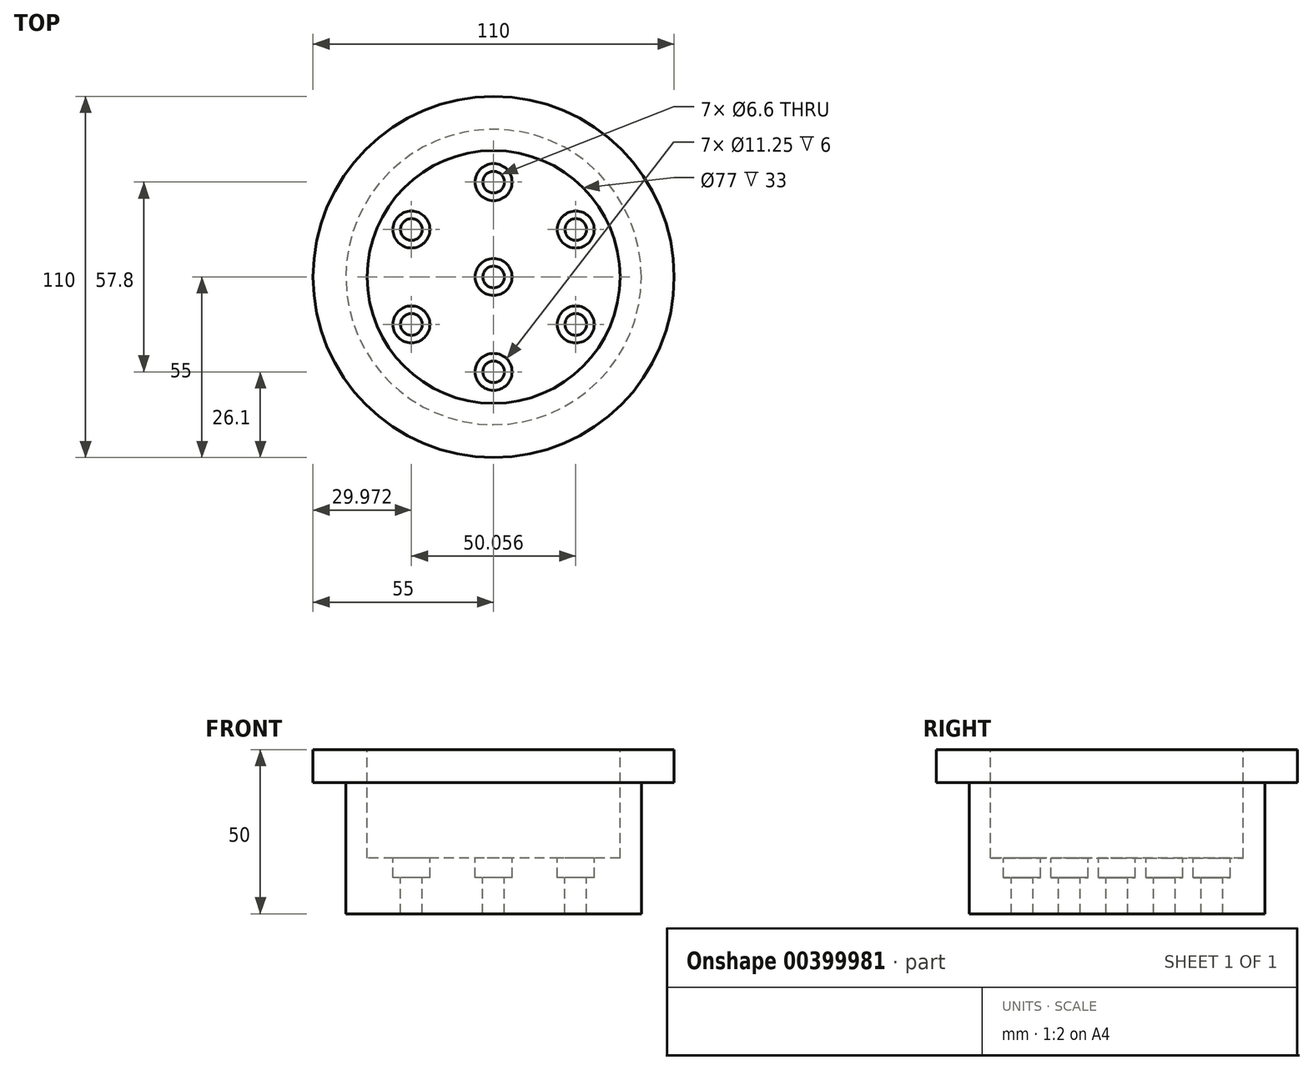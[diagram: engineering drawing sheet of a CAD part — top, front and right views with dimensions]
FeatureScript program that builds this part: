
annotation { "Feature Type Name" : "Feature", "Feature Type Description" : "" }
export const myFeature = defineFeature(function(context is Context, id is Id, definition is map)
    precondition{}
    {
        {
            var Q0;
            Q0=qCreatedBy(makeId("Top.planeOp"),FACE);
            var sketch = newSketch(context, id + "F0", { "sketchPlane" : qUnion([Q0])});
            skCircle(sketch, "E0", {"center": v(0, 0) * mm, "radius": 55 * mm});
            skCircle(sketch, "E1.cCircle", {"center": v(0, 0) * mm, "radius": 25.03 * mm, "construction": true});
            skLineSegment(sketch, "E1.0", {"start": v(25.03, -14.45) * mm, "end": v(0, -28.9) * mm});
            skLineSegment(sketch, "E1.1", {"start": v(0, -28.9) * mm, "end": v(-25.03, -14.45) * mm});
            skLineSegment(sketch, "E1.2", {"start": v(-25.03, -14.45) * mm, "end": v(-25.03, 14.45) * mm});
            skLineSegment(sketch, "E1.3", {"start": v(-25.03, 14.45) * mm, "end": v(0, 28.9) * mm});
            skLineSegment(sketch, "E1.4", {"start": v(0, 28.9) * mm, "end": v(25.03, 14.45) * mm});
            skLineSegment(sketch, "E1.5", {"start": v(25.03, 14.45) * mm, "end": v(25.03, -14.45) * mm});
            skPoint(sketch, "E1.0.midPoint", {"position": v(12.51, -21.67) * mm});
            skCircle(sketch, "E2", {"center": v(-25.03, 14.45) * mm, "radius": 3 * mm});
            skCircle(sketch, "E3", {"center": v(0, 28.9) * mm, "radius": 3 * mm});
            skCircle(sketch, "E4", {"center": v(25.03, 14.45) * mm, "radius": 3 * mm});
            skCircle(sketch, "E5", {"center": v(25.03, -14.45) * mm, "radius": 3 * mm});
            skCircle(sketch, "E6", {"center": v(0, -28.9) * mm, "radius": 3 * mm});
            skCircle(sketch, "E7", {"center": v(-25.03, -14.45) * mm, "radius": 3 * mm});
            skCircle(sketch, "E8", {"center": v(0, 0) * mm, "radius": 3 * mm});
            skSolve(sketch);
        }
        {
            var Q0;
            Q0=makeQuery(id+"F0.imprint","IMPRINT",FACE,{"disambiguationData":[TD([[makeQuery(id+"F0.imprint","IMPRINT",EDGE,{"derivedFrom":sQuery(id+"F0.wireOp",EDGE,"E0")}),1.0]])]});
            var Q1;
            Q1=makeQuery(id+"F0.imprint","IMPRINT",FACE,{"disambiguationData":[TD([[makeQuery(id+"F0.imprint","IMPRINT",EDGE,{"derivedFrom":sQuery(id+"F0.wireOp",EDGE,"E8")}),-1.0]])]});
            extrude(context, id + "F1", {"entities" : qUnion([Q0, Q1]), "depth" : 50 * mm, "offsetDistance" : 25 * mm});
        }
        {
            var Q0;
            Q0=makeQuery(id+"F1.opExtrude","CAP_FACE",FACE,{"disambiguationData":[OSD([sQuery(id+"F0.wireOp",EDGE,"E0")])],"isStart":false});
            var sketch = newSketch(context, id + "F2", { "sketchPlane" : qUnion([Q0])});
            skCircle(sketch, "E9", {"center": v(0, 0) * mm, "radius": 38.5 * mm});
            skSolve(sketch);
        }
        {
            var Q0;
            Q0=makeQuery(id+"F2.imprint","IMPRINT",FACE,{"disambiguationData":[TD([[makeQuery(id+"F2.imprint","IMPRINT",EDGE,{"derivedFrom":sQuery(id+"F2.wireOp",EDGE,"E9")}),1.0]])]});
            extrude(context, id + "F3", {"entities" : qUnion([Q0]), "operationType" : NewBodyOperationType.REMOVE, "oppositeDirection" : true, "depth" : 33 * mm, "offsetDistance" : 25 * mm});
        }
        {
            var Q0;
            Q0=makeQuery(id+"F3.boolean.opBoolean","COPY",FACE,{"derivedFrom":makeQuery(id+"F3.opExtrude","CAP_FACE",FACE,{"disambiguationData":[OSD([sQuery(id+"F0.wireOp",EDGE,"E2"),sQuery(id+"F0.wireOp",EDGE,"E3"),sQuery(id+"F0.wireOp",EDGE,"E4"),sQuery(id+"F0.wireOp",EDGE,"E5"),sQuery(id+"F0.wireOp",EDGE,"E6"),sQuery(id+"F0.wireOp",EDGE,"E7"),sQuery(id+"F0.wireOp",EDGE,"E8"),sQuery(id+"F2.wireOp",EDGE,"E9")])],"isStart":false})});
            var sketch = newSketch(context, id + "F4", { "sketchPlane" : qUnion([Q0])});
            skCircle(sketch, "E10.cCircle", {"center": v(0, 0) * mm, "radius": 25.03 * mm, "construction": true});
            skLineSegment(sketch, "E10.0", {"start": v(25.03, 14.45) * mm, "end": v(25.03, -14.45) * mm});
            skLineSegment(sketch, "E10.1", {"start": v(25.03, -14.45) * mm, "end": v(0, -28.9) * mm});
            skLineSegment(sketch, "E10.2", {"start": v(0, -28.9) * mm, "end": v(-25.03, -14.45) * mm});
            skLineSegment(sketch, "E10.3", {"start": v(-25.03, -14.45) * mm, "end": v(-25.03, 14.45) * mm});
            skLineSegment(sketch, "E10.4", {"start": v(-25.03, 14.45) * mm, "end": v(0, 28.9) * mm});
            skLineSegment(sketch, "E10.5", {"start": v(0, 28.9) * mm, "end": v(25.03, 14.45) * mm});
            skPoint(sketch, "E10.0.midPoint", {"position": v(25.03, 0) * mm});
            skSolve(sketch);
        }
        {
            var Q0;
            Q0=sQuery(id+"F4.wireOp",VERTEX,"E10.4.start");
            var Q1;
            Q1=sQuery(id+"F4.wireOp",VERTEX,"E10.3.start");
            var Q2;
            Q2=sQuery(id+"F4.wireOp",VERTEX,"E10.2.start");
            var Q3;
            Q3=sQuery(id+"F4.wireOp",VERTEX,"E10.1.start");
            var Q4;
            Q4=sQuery(id+"F4.wireOp",VERTEX,"E10.0.start");
            var Q5;
            Q5=sQuery(id+"F4.wireOp",VERTEX,"E10.5.start");
            var Q6;
            Q6=sQuery(id+"F4.wireOp",VERTEX,"E10.cCircle.center");
            var Q7;
            Q7=makeQuery(id+"F1.opExtrude","SWEPT_BODY",BODY,{"disambiguationData":[OSD([sQuery(id+"F0.wireOp",EDGE,"E0"),sQuery(id+"F0.wireOp",EDGE,"E2"),sQuery(id+"F0.wireOp",EDGE,"E3"),sQuery(id+"F0.wireOp",EDGE,"E4"),sQuery(id+"F0.wireOp",EDGE,"E5"),sQuery(id+"F0.wireOp",EDGE,"E6"),sQuery(id+"F0.wireOp",EDGE,"E7"),sQuery(id+"F0.wireOp",EDGE,"E8")])]});
            hole(context, id + "F5", {"style" : HoleStyle.C_BORE, "endStyle" : HoleEndStyle.THROUGH, "standardTappedOrClearance" : lookupTablePath({ "standard" : "ISO", "fit" : "Normal", "size" : "M6", "type" : "Clearance" }), "standardBlindInLast" : lookupTablePath({ "fit" : "Standard", "standard" : "ISO", "size" : "M6", "type" : "Clearance" }), "holeDiameter" : 6.6 * mm, "cBoreDiameter" : 11.25 * mm, "cBoreDepth" : 6 * mm, "isTappedThrough" : true, "tappedDepth" : 12 * mm, "tapClearance" : 3, "locations" : qUnion([Q0, Q1, Q2, Q3, Q4, Q5, Q6]), "scope" : qUnion([Q7])});
        }
        {
            var Q0;
            Q0=makeQuery(id+"F1.opExtrude","CAP_FACE",FACE,{"disambiguationData":[OSD([sQuery(id+"F0.wireOp",EDGE,"E0"),sQuery(id+"F0.wireOp",EDGE,"E2"),sQuery(id+"F0.wireOp",EDGE,"E3"),sQuery(id+"F0.wireOp",EDGE,"E4"),sQuery(id+"F0.wireOp",EDGE,"E5"),sQuery(id+"F0.wireOp",EDGE,"E6"),sQuery(id+"F0.wireOp",EDGE,"E7"),sQuery(id+"F0.wireOp",EDGE,"E8")])],"isStart":true});
            var sketch = newSketch(context, id + "F6", { "sketchPlane" : qUnion([Q0])});
            skCircle(sketch, "E11", {"center": v(0, 0) * mm, "radius": 45 * mm});
            skCircle(sketch, "E12", {"center": v(0, 0) * mm, "radius": 57.5 * mm});
            skSolve(sketch);
        }
        {
            var Q0;
            Q0 = qSketchRegion(id + "F6", true);
            extrude(context, id + "F7", {"entities" : qUnion([Q0]), "operationType" : NewBodyOperationType.REMOVE, "oppositeDirection" : true, "depth" : 40 * mm, "offsetDistance" : 25 * mm});
        }
    });
